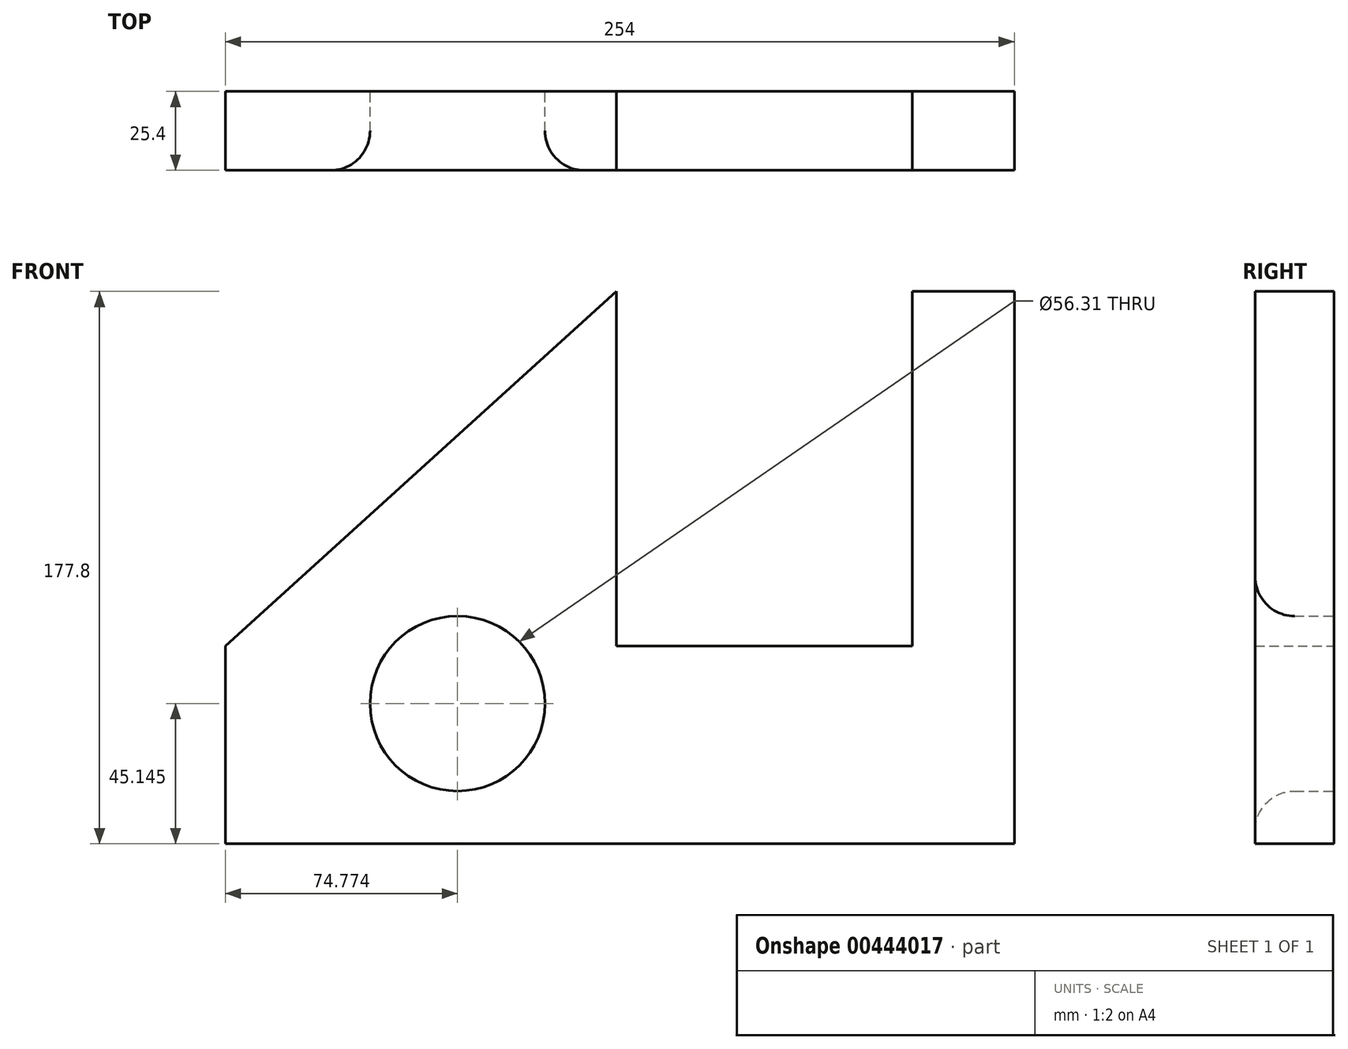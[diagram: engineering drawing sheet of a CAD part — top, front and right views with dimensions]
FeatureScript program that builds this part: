
annotation { "Feature Type Name" : "Feature", "Feature Type Description" : "" }
export const myFeature = defineFeature(function(context is Context, id is Id, definition is map)
    precondition{}
    {
        {
            var Q0;
            Q0=qCreatedBy(makeId("Front.planeOp"),FACE);
            var sketch = newSketch(context, id + "F0", { "sketchPlane" : qUnion([Q0])});
            skLineSegment(sketch, "E0", {"start": v(0, 0) * mm, "end": v(254, 0) * mm});
            skLineSegment(sketch, "E1", {"start": v(254, 0) * mm, "end": v(254, 177.8) * mm});
            skLineSegment(sketch, "E2", {"start": v(254, 177.8) * mm, "end": v(221.14, 177.8) * mm});
            skLineSegment(sketch, "E3", {"start": v(221.14, 177.8) * mm, "end": v(221.14, 63.72) * mm});
            skLineSegment(sketch, "E4", {"start": v(221.14, 63.72) * mm, "end": v(125.88, 63.72) * mm});
            skLineSegment(sketch, "E5", {"start": v(125.88, 63.72) * mm, "end": v(125.88, 177.8) * mm});
            skLineSegment(sketch, "E6", {"start": v(125.88, 177.8) * mm, "end": v(0, 63.72) * mm});
            skLineSegment(sketch, "E7", {"start": v(0, 63.72) * mm, "end": v(0, 0) * mm});
            skSolve(sketch);
        }
        {
            var Q0;
            Q0 = qSketchRegion(id + "F0", true);
            extrude(context, id + "F1", {"entities" : qUnion([Q0]), "depth" : 25.4 * mm});
        }
        {
            var Q0;
            Q0=makeQuery(id+"F1.opExtrude","CAP_FACE",FACE,{"disambiguationData":[OSD([sQuery(id+"F0.wireOp",EDGE,"E0"),sQuery(id+"F0.wireOp",EDGE,"E1"),sQuery(id+"F0.wireOp",EDGE,"E2"),sQuery(id+"F0.wireOp",EDGE,"E3"),sQuery(id+"F0.wireOp",EDGE,"E4"),sQuery(id+"F0.wireOp",EDGE,"E5"),sQuery(id+"F0.wireOp",EDGE,"E6"),sQuery(id+"F0.wireOp",EDGE,"E7")])],"isStart":true});
            var sketch = newSketch(context, id + "F2", { "sketchPlane" : qUnion([Q0])});
            skCircle(sketch, "E8", {"center": v(-74.77, 45.15) * mm, "radius": 28.15 * mm});
            skSolve(sketch);
        }
        {
            var Q0;
            Q0 = qSketchRegion(id + "F2", true);
            extrude(context, id + "F3", {"entities" : qUnion([Q0]), "operationType" : NewBodyOperationType.REMOVE, "endBound" : BoundingType.THROUGH_ALL, "oppositeDirection" : true, "depth" : 25.4 * mm});
        }
        {
            var Q0;
            Q0=makeQuery(id+"F3.boolean.opBoolean","COPY",EDGE,{"derivedFrom":makeQuery(id+"F3.opExtrude","CAP_EDGE",EDGE,{"disambiguationData":[OSD([sQuery(id+"F2.wireOp",EDGE,"E8")])],"isStart":true})});
            var Q1;
            Q1=makeQuery(id+"F3.boolean.opBoolean","INTERSECT",EDGE,{"derivedFrom":[makeQuery(id+"F1.opExtrude","CAP_FACE",FACE,{"disambiguationData":[OSD([sQuery(id+"F0.wireOp",EDGE,"E0"),sQuery(id+"F0.wireOp",EDGE,"E1"),sQuery(id+"F0.wireOp",EDGE,"E2"),sQuery(id+"F0.wireOp",EDGE,"E3"),sQuery(id+"F0.wireOp",EDGE,"E4"),sQuery(id+"F0.wireOp",EDGE,"E5"),sQuery(id+"F0.wireOp",EDGE,"E6"),sQuery(id+"F0.wireOp",EDGE,"E7")])],"isStart":false}),makeQuery(id+"F3.opExtrude","SWEPT_FACE",FACE,{"disambiguationData":[OSD([sQuery(id+"F2.wireOp",EDGE,"E8")])]})]});
            fillet(context, id + "F4", {"entities" : qUnion([Q0, Q1]), "radius" : 12.7 * mm, "tangentPropagation" : true, "allowEdgeOverflow" : false});
        }
    });
